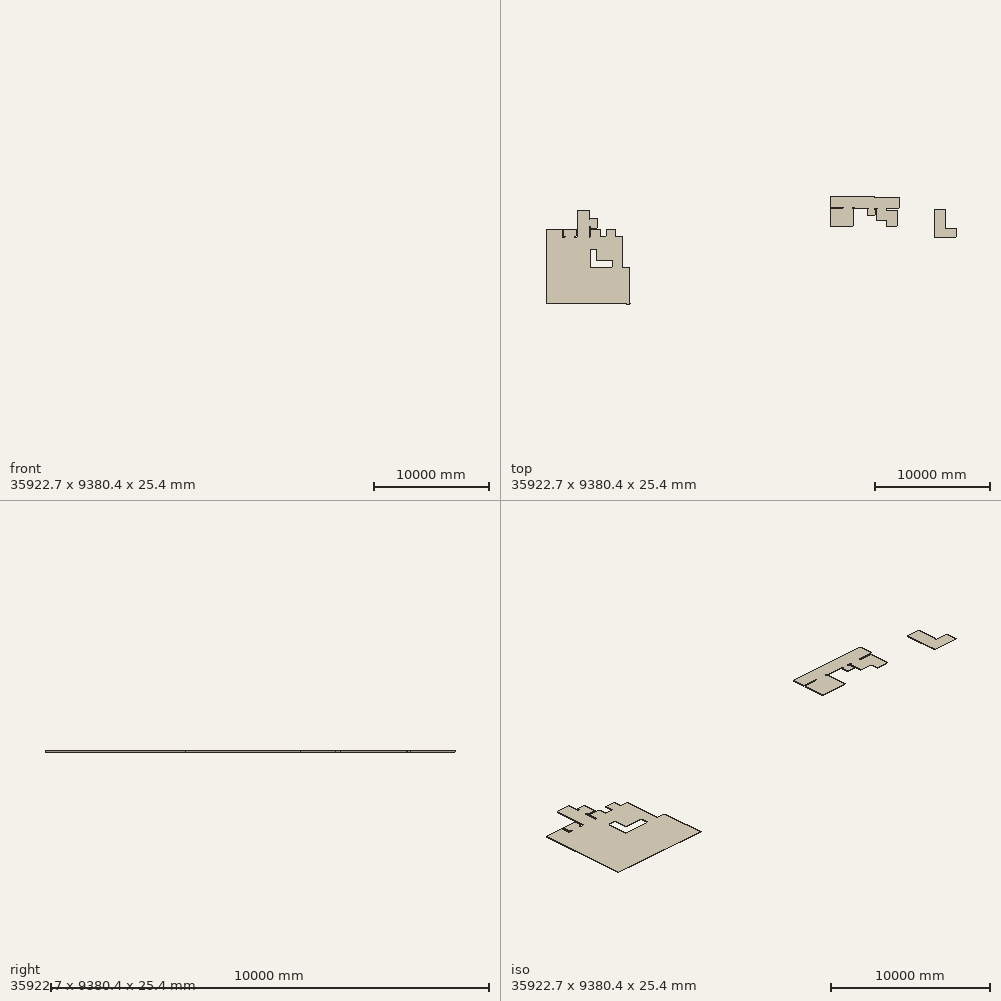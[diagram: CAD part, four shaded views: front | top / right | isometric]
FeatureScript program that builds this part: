
annotation { "Feature Type Name" : "Feature", "Feature Type Description" : "" }
export const myFeature = defineFeature(function(context is Context, id is Id, definition is map)
    precondition{}
    {
        {
            var Q0;
            Q0=qCreatedBy(makeId("Top.planeOp"),FACE);
            var sketch = newSketch(context, id + "F0", { "sketchPlane" : qUnion([Q0])});
            skLineSegment(sketch, "E0.bottom", {"start": v(0, 0) * mm, "end": v(848.07, 0) * mm});
            skLineSegment(sketch, "E0.top", {"start": v(0, 487.7) * mm, "end": v(848.07, 487.7) * mm});
            skLineSegment(sketch, "E0.left", {"start": v(0, 0) * mm, "end": v(0, 487.7) * mm});
            skLineSegment(sketch, "E0.right", {"start": v(848.07, 0) * mm, "end": v(848.07, 487.7) * mm});
            skLineSegment(sketch, "E1", {"start": v(7068.24, -8777.84) * mm, "end": v(14383.06, -8851.92) * mm});
            skLineSegment(sketch, "E2", {"start": v(14383.06, -8851.92) * mm, "end": v(14309, -5638.95) * mm});
            skLineSegment(sketch, "E3", {"start": v(14309, -5638.95) * mm, "end": v(13704.9, -5638.95) * mm});
            skLineSegment(sketch, "E4", {"start": v(13704.9, -5638.95) * mm, "end": v(13690.4, -2955.8) * mm});
            skLineSegment(sketch, "E5", {"start": v(13690.4, -2955.8) * mm, "end": v(13111, -2958.93) * mm});
            skLineSegment(sketch, "E6", {"start": v(13111, -2958.93) * mm, "end": v(13107.77, -2360.98) * mm});
            skLineSegment(sketch, "E7", {"start": v(13107.77, -2360.98) * mm, "end": v(12360.21, -2365.02) * mm});
            skLineSegment(sketch, "E8", {"start": v(12360.21, -2365.02) * mm, "end": v(12363.43, -2958.93) * mm});
            skLineSegment(sketch, "E9", {"start": v(12363.43, -2958.93) * mm, "end": v(11787.9, -2958.93) * mm});
            skLineSegment(sketch, "E10", {"start": v(11787.9, -2958.93) * mm, "end": v(11787.9, -2365.02) * mm});
            skLineSegment(sketch, "E11", {"start": v(11787.9, -2365.02) * mm, "end": v(10901.97, -2365.02) * mm});
            skLineSegment(sketch, "E12", {"start": v(10901.97, -2365.02) * mm, "end": v(10901.97, -3040.07) * mm});
            skLineSegment(sketch, "E13", {"start": v(10901.97, -3040.07) * mm, "end": v(10810.31, -3040.07) * mm});
            skLineSegment(sketch, "E14", {"start": v(10810.31, -3040.07) * mm, "end": v(10810.31, -2087.44) * mm});
            skLineSegment(sketch, "E15", {"start": v(10810.31, -2087.44) * mm, "end": v(10901.97, -2087.44) * mm});
            skLineSegment(sketch, "E16", {"start": v(10901.97, -2087.44) * mm, "end": v(10901.97, -2251.12) * mm});
            skLineSegment(sketch, "E17", {"start": v(10901.97, -2251.12) * mm, "end": v(11537.06, -2251.12) * mm});
            skLineSegment(sketch, "E18", {"start": v(11537.06, -2251.12) * mm, "end": v(11537.06, -1314.86) * mm});
            skLineSegment(sketch, "E19", {"start": v(11537.06, -1314.86) * mm, "end": v(10901.97, -1314.86) * mm});
            skLineSegment(sketch, "E20", {"start": v(10901.97, -1314.86) * mm, "end": v(10901.97, -1481.81) * mm});
            skLineSegment(sketch, "E21", {"start": v(10901.97, -1481.81) * mm, "end": v(10810.31, -1481.81) * mm});
            skLineSegment(sketch, "E22", {"start": v(10810.31, -1481.81) * mm, "end": v(10810.31, -632.9) * mm});
            skLineSegment(sketch, "E23", {"start": v(10810.31, -632.9) * mm, "end": v(9742.08, -632.9) * mm});
            skLineSegment(sketch, "E24", {"start": v(9742.08, -632.9) * mm, "end": v(9742.08, -3040.07) * mm});
            skLineSegment(sketch, "E25", {"start": v(9742.08, -3040.07) * mm, "end": v(9480.56, -3040.07) * mm});
            skLineSegment(sketch, "E26", {"start": v(9480.56, -3040.07) * mm, "end": v(9480.56, -2925.99) * mm});
            skLineSegment(sketch, "E27", {"start": v(9480.56, -2925.99) * mm, "end": v(9653.99, -2925.99) * mm});
            skLineSegment(sketch, "E28", {"start": v(9653.99, -2925.99) * mm, "end": v(9653.99, -2365.02) * mm});
            skLineSegment(sketch, "E29", {"start": v(9653.99, -2365.02) * mm, "end": v(8569.38, -2365.02) * mm});
            skLineSegment(sketch, "E30", {"start": v(8569.38, -2365.02) * mm, "end": v(8569.38, -2925.99) * mm});
            skLineSegment(sketch, "E31", {"start": v(8569.38, -2925.99) * mm, "end": v(8740.06, -2925.99) * mm});
            skLineSegment(sketch, "E32", {"start": v(8740.06, -2925.99) * mm, "end": v(8740.06, -3040.07) * mm});
            skLineSegment(sketch, "E33", {"start": v(8740.06, -3040.07) * mm, "end": v(8456.52, -3040.07) * mm});
            skLineSegment(sketch, "E34", {"start": v(8456.52, -3040.07) * mm, "end": v(8456.52, -2365.02) * mm});
            skLineSegment(sketch, "E35", {"start": v(8456.52, -2365.02) * mm, "end": v(7066.36, -2365.02) * mm});
            skLineSegment(sketch, "E36", {"start": v(7066.36, -2365.02) * mm, "end": v(7068.24, -8777.84) * mm});
            skLineSegment(sketch, "E37", {"start": v(10901.97, -4051.88) * mm, "end": v(10901.97, -5638.95) * mm});
            skLineSegment(sketch, "E38", {"start": v(10901.97, -5638.95) * mm, "end": v(12849.99, -5638.95) * mm});
            skLineSegment(sketch, "E39", {"start": v(12849.99, -5638.95) * mm, "end": v(12849.99, -5048.4) * mm});
            skLineSegment(sketch, "E40", {"start": v(12849.99, -5048.4) * mm, "end": v(11490.1, -5048.4) * mm});
            skLineSegment(sketch, "E41", {"start": v(11490.1, -5048.4) * mm, "end": v(11490.1, -4073.9) * mm});
            skLineSegment(sketch, "E42", {"start": v(11490.1, -4073.9) * mm, "end": v(10901.97, -4051.88) * mm});
            skLineSegment(sketch, "E43", {"start": v(7663.61, 405.84) * mm, "end": v(7663.61, -526.75) * mm});
            skLineSegment(sketch, "E44", {"start": v(7663.61, -526.75) * mm, "end": v(8741.91, -526.75) * mm});
            skLineSegment(sketch, "E45", {"start": v(8741.91, -526.75) * mm, "end": v(8741.91, -614.18) * mm});
            skLineSegment(sketch, "E46", {"start": v(8741.91, -614.18) * mm, "end": v(7663.61, -614.18) * mm});
            skLineSegment(sketch, "E47", {"start": v(7663.61, -614.18) * mm, "end": v(7663.61, -2198.85) * mm});
            skLineSegment(sketch, "E48", {"start": v(7663.61, -2198.85) * mm, "end": v(9645.36, -2198.85) * mm});
            skLineSegment(sketch, "E49", {"start": v(9645.36, -2198.85) * mm, "end": v(9645.36, -614.18) * mm});
            skLineSegment(sketch, "E50", {"start": v(9645.36, -614.18) * mm, "end": v(9536.07, -614.18) * mm});
            skLineSegment(sketch, "E51", {"start": v(9536.07, -614.18) * mm, "end": v(9536.07, -526.75) * mm});
            skLineSegment(sketch, "E52", {"start": v(9536.07, -526.75) * mm, "end": v(9740.07, -526.75) * mm});
            skLineSegment(sketch, "E53", {"start": v(9740.07, -526.75) * mm, "end": v(9742.08, -632.9) * mm});
            skLineSegment(sketch, "E54", {"start": v(10989.6, -632.9) * mm, "end": v(10989.6, -716.18) * mm});
            skLineSegment(sketch, "E55", {"start": v(10989.6, -716.18) * mm, "end": v(10894.88, -716.18) * mm});
            skLineSegment(sketch, "E56", {"start": v(10894.88, -716.18) * mm, "end": v(10894.88, -1215.26) * mm});
            skLineSegment(sketch, "E57", {"start": v(10894.88, -1215.26) * mm, "end": v(11536.03, -1215.26) * mm});
            skLineSegment(sketch, "E58", {"start": v(11536.03, -1215.26) * mm, "end": v(11526.6, -716.18) * mm});
            skLineSegment(sketch, "E59", {"start": v(11526.6, -716.18) * mm, "end": v(11426.74, -716.18) * mm});
            skLineSegment(sketch, "E60", {"start": v(11426.74, -716.18) * mm, "end": v(11425.17, -632.9) * mm});
            skLineSegment(sketch, "E61", {"start": v(11425.17, -632.9) * mm, "end": v(11740.03, -632.9) * mm});
            skLineSegment(sketch, "E62", {"start": v(11740.03, -632.9) * mm, "end": v(11741.6, -716.18) * mm});
            skLineSegment(sketch, "E63", {"start": v(11741.6, -716.18) * mm, "end": v(11619.82, -716.18) * mm});
            skLineSegment(sketch, "E64", {"start": v(11619.82, -716.18) * mm, "end": v(11637.7, -1663.62) * mm});
            skLineSegment(sketch, "E65", {"start": v(11637.7, -1663.62) * mm, "end": v(12523.26, -1663.62) * mm});
            skLineSegment(sketch, "E66", {"start": v(12523.26, -1663.62) * mm, "end": v(12533.56, -2209.37) * mm});
            skLineSegment(sketch, "E67", {"start": v(12533.56, -2209.37) * mm, "end": v(13430.35, -2209.37) * mm});
            skLineSegment(sketch, "E68", {"start": v(13430.35, -2209.37) * mm, "end": v(13430.35, -716.18) * mm});
            skLineSegment(sketch, "E69", {"start": v(13430.35, -716.18) * mm, "end": v(12479.55, -716.18) * mm});
            skLineSegment(sketch, "E70", {"start": v(12479.55, -716.18) * mm, "end": v(12477.97, -632.9) * mm});
            skLineSegment(sketch, "E71", {"start": v(12477.97, -632.9) * mm, "end": v(13601.56, -632.9) * mm});
            skLineSegment(sketch, "E72", {"start": v(13601.56, -632.9) * mm, "end": v(13601.56, 395.62) * mm});
            skLineSegment(sketch, "E73", {"start": v(13601.56, 395.62) * mm, "end": v(7663.61, 405.84) * mm});
            skSolve(sketch);
        }
        {
            var Q0;
            Q0=qCreatedBy(makeId("Top.planeOp"),FACE);
            var sketch = newSketch(context, id + "F1", { "sketchPlane" : qUnion([Q0])});
            skLineSegment(sketch, "E74", {"start": v(31973.02, 528.43) * mm, "end": v(31973.02, -410.5) * mm});
            skLineSegment(sketch, "E75", {"start": v(31973.02, -410.5) * mm, "end": v(33064.8, -410.5) * mm});
            skLineSegment(sketch, "E76", {"start": v(33064.8, -410.5) * mm, "end": v(33064.8, -506.58) * mm});
            skLineSegment(sketch, "E77", {"start": v(33064.8, -506.58) * mm, "end": v(31973.02, -506.58) * mm});
            skLineSegment(sketch, "E78", {"start": v(31973.02, -506.58) * mm, "end": v(31973.02, -2100.58) * mm});
            skLineSegment(sketch, "E79", {"start": v(31973.02, -2100.58) * mm, "end": v(33981.9, -2100.58) * mm});
            skLineSegment(sketch, "E80", {"start": v(33981.9, -2100.58) * mm, "end": v(33981.9, -506.58) * mm});
            skLineSegment(sketch, "E81", {"start": v(33981.9, -506.58) * mm, "end": v(33863.98, -506.58) * mm});
            skLineSegment(sketch, "E82", {"start": v(33863.98, -506.58) * mm, "end": v(33863.98, -410.5) * mm});
            skLineSegment(sketch, "E83", {"start": v(33863.98, -410.5) * mm, "end": v(34069.23, -410.5) * mm});
            skLineSegment(sketch, "E84", {"start": v(34069.23, -410.5) * mm, "end": v(34069.23, -506.58) * mm});
            skLineSegment(sketch, "E85", {"start": v(34069.23, -506.58) * mm, "end": v(35322.6, -506.58) * mm});
            skLineSegment(sketch, "E86", {"start": v(35322.6, -506.58) * mm, "end": v(35322.6, -602.66) * mm});
            skLineSegment(sketch, "E87", {"start": v(35322.6, -602.66) * mm, "end": v(35230.88, -602.66) * mm});
            skLineSegment(sketch, "E88", {"start": v(35230.88, -602.66) * mm, "end": v(35230.88, -1100.5) * mm});
            skLineSegment(sketch, "E89", {"start": v(35230.88, -1100.5) * mm, "end": v(35877.22, -1100.5) * mm});
            skLineSegment(sketch, "E90", {"start": v(35877.22, -1100.5) * mm, "end": v(35877.22, -611.4) * mm});
            skLineSegment(sketch, "E91", {"start": v(35877.22, -611.4) * mm, "end": v(35776.77, -611.4) * mm});
            skLineSegment(sketch, "E92", {"start": v(35776.77, -611.4) * mm, "end": v(35776.77, -506.58) * mm});
            skLineSegment(sketch, "E93", {"start": v(35776.77, -506.58) * mm, "end": v(36078.1, -506.58) * mm});
            skLineSegment(sketch, "E94", {"start": v(36078.1, -506.58) * mm, "end": v(36078.1, -602.66) * mm});
            skLineSegment(sketch, "E95", {"start": v(36078.1, -602.66) * mm, "end": v(35964.56, -602.66) * mm});
            skLineSegment(sketch, "E96", {"start": v(35964.56, -602.66) * mm, "end": v(35964.56, -1554.69) * mm});
            skLineSegment(sketch, "E97", {"start": v(35964.56, -1554.69) * mm, "end": v(36877.29, -1554.69) * mm});
            skLineSegment(sketch, "E98", {"start": v(36877.29, -1554.69) * mm, "end": v(36877.29, -2100.58) * mm});
            skLineSegment(sketch, "E99", {"start": v(36877.29, -2100.58) * mm, "end": v(37781.28, -2100.58) * mm});
            skLineSegment(sketch, "E100", {"start": v(37781.28, -2100.58) * mm, "end": v(37781.28, -620.13) * mm});
            skLineSegment(sketch, "E101", {"start": v(37781.28, -620.13) * mm, "end": v(36833.62, -620.13) * mm});
            skLineSegment(sketch, "E102", {"start": v(36833.62, -620.13) * mm, "end": v(36833.62, -506.58) * mm});
            skLineSegment(sketch, "E103", {"start": v(36833.62, -506.58) * mm, "end": v(37951.6, -506.58) * mm});
            skLineSegment(sketch, "E104", {"start": v(37951.6, -506.58) * mm, "end": v(37951.6, 524.06) * mm});
            skLineSegment(sketch, "E105", {"start": v(37951.6, 524.06) * mm, "end": v(31973.02, 528.43) * mm});
            skLineSegment(sketch, "E106", {"start": v(31383.47, -8526.18) * mm, "end": v(38698.67, -8526.18) * mm});
            skSolve(sketch);
        }
        {
            var Q0;
            Q0 = qSketchRegion(id + "F1", true);
            extrude(context, id + "F2", {"entities" : qUnion([Q0]), "depth" : 25.4 * mm, "offsetDistance" : 25.4 * mm});
        }
        {
            var Q0;
            Q0=makeQuery(id+"F0.imprint","IMPRINT",FACE,{"disambiguationData":[TD([[makeQuery(id+"F0.imprint","IMPRINT",EDGE,{"derivedFrom":sQuery(id+"F0.wireOp",EDGE,"E1")}),1.0]])]});
            extrude(context, id + "F3", {"entities" : qUnion([Q0]), "depth" : 25.4 * mm, "offsetDistance" : 25.4 * mm});
        }
        {
            var Q0;
            Q0=qCreatedBy(makeId("Top.planeOp"),FACE);
            var sketch = newSketch(context, id + "F4", { "sketchPlane" : qUnion([Q0])});
            skLineSegment(sketch, "E107", {"start": v(41163.41, -575.1) * mm, "end": v(41035.97, -575.1) * mm});
            skLineSegment(sketch, "E108", {"start": v(41035.97, -575.1) * mm, "end": v(41080.08, -3021) * mm});
            skLineSegment(sketch, "E109", {"start": v(41080.08, -3021) * mm, "end": v(42989.09, -3021) * mm});
            skLineSegment(sketch, "E110", {"start": v(42989.09, -3021) * mm, "end": v(42974.46, -2210) * mm});
            skLineSegment(sketch, "E111", {"start": v(42974.46, -2210) * mm, "end": v(41999.88, -2210) * mm});
            skLineSegment(sketch, "E112", {"start": v(41999.88, -2210) * mm, "end": v(41998.1, -2111.36) * mm});
            skLineSegment(sketch, "E113", {"start": v(41998.1, -2111.36) * mm, "end": v(42061.68, -2110.21) * mm});
            skLineSegment(sketch, "E114", {"start": v(42061.68, -2110.21) * mm, "end": v(42061.68, -586.21) * mm});
            skLineSegment(sketch, "E115", {"start": v(42061.68, -586.21) * mm, "end": v(41163.41, -575.1) * mm});
            skSolve(sketch);
        }
        {
            var Q0;
            Q0 = qSketchRegion(id + "F4", true);
            extrude(context, id + "F5", {"entities" : qUnion([Q0]), "depth" : 25.4 * mm, "offsetDistance" : 25.4 * mm});
        }
    });
